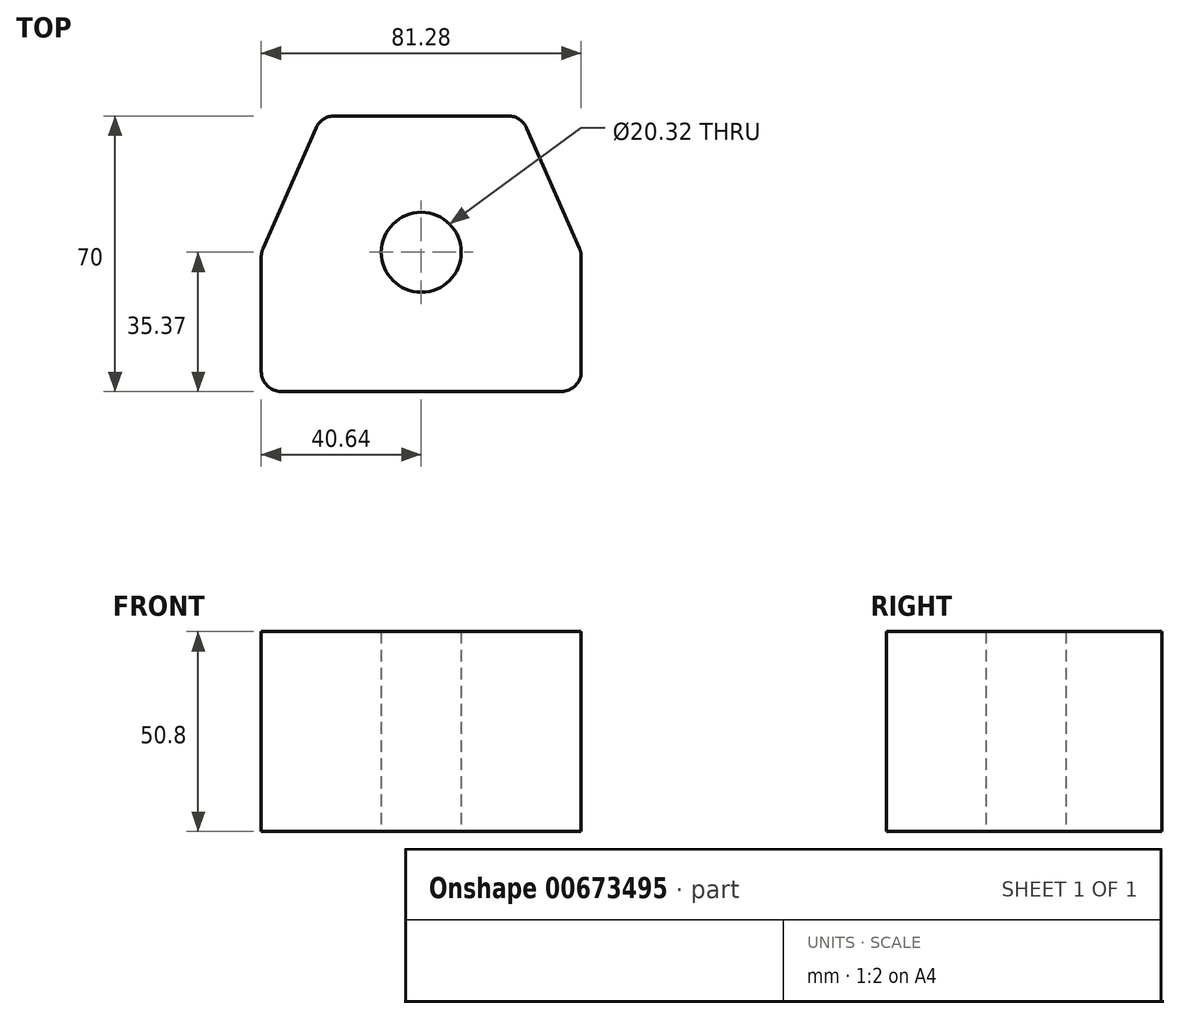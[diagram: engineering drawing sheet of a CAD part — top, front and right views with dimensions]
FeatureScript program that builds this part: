
annotation { "Feature Type Name" : "Feature", "Feature Type Description" : "" }
export const myFeature = defineFeature(function(context is Context, id is Id, definition is map)
    precondition{}
    {
        {
            var Q0;
            Q0=qCreatedBy(makeId("Top.planeOp"),FACE);
            var sketch = newSketch(context, id + "F0", { "sketchPlane" : qUnion([Q0])});
            skLineSegment(sketch, "E0", {"start": v(0, 0) * mm, "end": v(-40.64, 0) * mm});
            skLineSegment(sketch, "E1", {"start": v(-40.64, 0) * mm, "end": v(-40.64, 35.37) * mm});
            skLineSegment(sketch, "E2", {"start": v(-40.64, 35.37) * mm, "end": v(-25.4, 70) * mm});
            skLineSegment(sketch, "E3", {"start": v(-25.4, 70) * mm, "end": v(25.4, 70) * mm});
            skLineSegment(sketch, "E4", {"start": v(25.4, 70) * mm, "end": v(40.64, 35.37) * mm});
            skLineSegment(sketch, "E5", {"start": v(40.64, 35.37) * mm, "end": v(40.64, 0) * mm});
            skLineSegment(sketch, "E6", {"start": v(40.64, 0) * mm, "end": v(0, 0) * mm});
            skCircle(sketch, "E7", {"center": v(0, 35.37) * mm, "radius": 10.16 * mm});
            skPoint(sketch, "E7.centerSnap0", {"position": v(0, 70) * mm});
            skSolve(sketch);
        }
        {
            var Q0;
            Q0=makeQuery(id+"F0.imprint","IMPRINT",FACE,{"disambiguationData":[TD([[makeQuery(id+"F0.imprint","IMPRINT",EDGE,{"derivedFrom":sQuery(id+"F0.wireOp",EDGE,"E0")}),-1.0]])]});
            extrude(context, id + "F1", {"entities" : qUnion([Q0]), "depth" : 50.8 * mm, "offsetDistance" : 25.4 * mm});
        }
        {
            var Q0;
            Q0=makeQuery(id+"F1.opExtrude","SWEPT_EDGE",EDGE,{"disambiguationData":[OSD([sQuery(id+"F0.wireOp",EDGE,"E5"),sQuery(id+"F0.wireOp",EDGE,"E6")])]});
            var Q1;
            Q1=makeQuery(id+"F1.opExtrude","SWEPT_EDGE",EDGE,{"disambiguationData":[OSD([sQuery(id+"F0.wireOp",EDGE,"E4"),sQuery(id+"F0.wireOp",EDGE,"E5")])]});
            var Q2;
            Q2=makeQuery(id+"F1.opExtrude","SWEPT_EDGE",EDGE,{"disambiguationData":[OSD([sQuery(id+"F0.wireOp",EDGE,"E3"),sQuery(id+"F0.wireOp",EDGE,"E4")])]});
            var Q3;
            Q3=makeQuery(id+"F1.opExtrude","SWEPT_EDGE",EDGE,{"disambiguationData":[OSD([sQuery(id+"F0.wireOp",EDGE,"E2"),sQuery(id+"F0.wireOp",EDGE,"E3")])]});
            var Q4;
            Q4=makeQuery(id+"F1.opExtrude","SWEPT_EDGE",EDGE,{"disambiguationData":[OSD([sQuery(id+"F0.wireOp",EDGE,"E1"),sQuery(id+"F0.wireOp",EDGE,"E2")])]});
            var Q5;
            Q5=makeQuery(id+"F1.opExtrude","SWEPT_EDGE",EDGE,{"disambiguationData":[OSD([sQuery(id+"F0.wireOp",EDGE,"E0"),sQuery(id+"F0.wireOp",EDGE,"E1")])]});
            fillet(context, id + "F2", {"entities" : qUnion([Q0, Q1, Q2, Q3, Q4, Q5]), "radius" : 5.08 * mm, "tangentPropagation" : true, "allowEdgeOverflow" : false});
        }
    });
